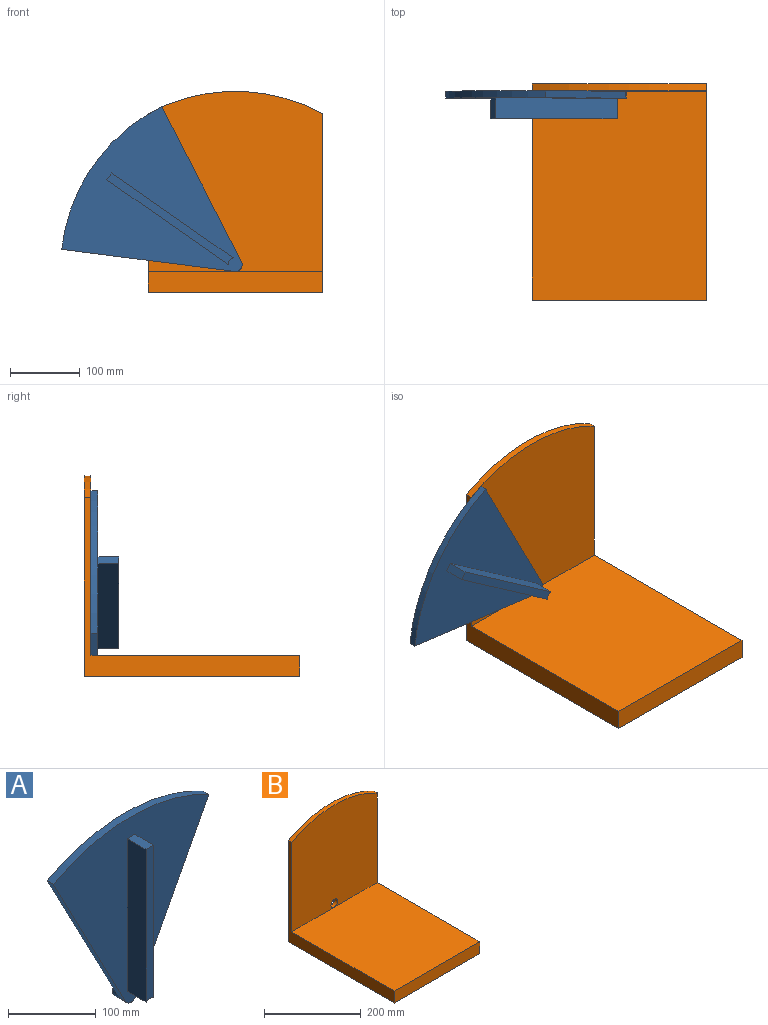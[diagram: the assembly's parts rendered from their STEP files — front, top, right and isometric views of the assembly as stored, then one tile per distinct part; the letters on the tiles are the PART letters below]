
ASSEMBLY  parts=2 mates=1
PART A: 12 faces, bbox 250x50x258.6 mm
  f0: plane 221.16x116.15mm, normal (-0.89,0,-0.46), area 2498mm2, adj f1,f3,f4,f5
  f1: cylinder r=10mm len=20mm, axis (0,1,0), area 845.8mm2, adj f0,f2,f4,f5,f11
  f2: plane 221.16x116.15mm, normal (0.89,0,-0.46), area 2498mm2, adj f1,f3,f4,f5
  f3: cylinder r=259.69mm len=250mm, axis (0,1,0), area 2608.3mm2, adj f0,f2,f4,f5
  f4: plane 258.57x250mm, normal (0,-1,0), area 32548.5mm2, adj f0,f1,f2,f3,f6,f7,f8,f9
  f5: plane 253.22x250mm, normal (0,1,0), area 34769.3mm2, adj f0,f1,f2,f3
  f6: plane 30x12mm, normal (0,0,1), area 360mm2, adj f4,f7,f9,f10
  f7: plane 212.61x30mm, normal (-1,0,0), area 6378.3mm2, adj f4,f6,f8,f10
  f8: cylinder r=10mm len=30mm, axis (0,1,0), area 386.1mm2, adj f4,f7,f9,f10
  f9: plane 212.61x30mm, normal (1,0,0), area 6378.3mm2, adj f4,f6,f8,f10
  f10: plane 212.61x12mm, normal (0,-1,0), area 2535mm2, adj f6,f7,f8,f9
  f11: plane 20x20mm, normal (0,1,0), area 314.2mm2, adj f1
PART B: 9 faces, bbox 250x310x288.6 mm
  f0: plane 300x250mm, normal (0,0,1), area 75000mm2, adj f1,f3,f4,f5
  f1: plane 310x256.51mm, normal (-1,0,0), area 11565.1mm2, adj f0,f2,f4,f5,f6,f8
  f2: plane 310x250mm, normal (0,0,-1), area 77500mm2, adj f1,f3,f4,f8
  f3: plane 310x256.51mm, normal (1,0,0), area 11565.1mm2, adj f0,f2,f4,f5,f6,f8
  f4: plane 250x30mm, normal (0,-1,0), area 7500mm2, adj f0,f1,f2,f3
  f5: plane 258.57x250mm, normal (0,-1,0), area 61725.9mm2, adj f0,f1,f3,f6,f7
  f6: cylinder r=259.69mm len=250mm, axis (0,-1,0), area 2608.3mm2, adj f1,f3,f5,f8
  f7: cylinder r=10mm len=20mm, axis (0,-1,0), area 628.3mm2, adj f5,f8
  f8: plane 288.57x250mm, normal (0,1,0), area 69225.9mm2, adj f1,f2,f3,f6,f7
PLACE A rot(axis=(0,-1,0),55deg) t=(-131.08,-21.02,-69.69)mm
PLACE B t=(-40.98,-21.02,-22.78)mm fixed
MATE revolute A.f1 <-> B.f7  axis (0,1,0) through (-40.98,-11.02,-132.78)mm
